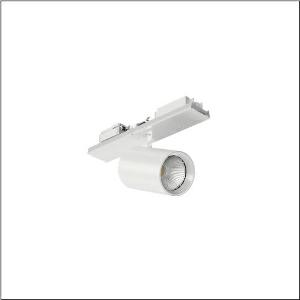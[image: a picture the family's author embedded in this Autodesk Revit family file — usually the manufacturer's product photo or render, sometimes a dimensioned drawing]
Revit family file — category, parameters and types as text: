
# Revit family: licross_spot_31_51sl127a43b
name_source: partatom
category: Lighting Fixtures
units: mm (PartAtom-declared; Revit-internal decimal feet)

## family parameters
Cut with Voids When Loaded = No
Host = Face
Light Source = No
Part Type = Normal
Room Calculation Point = No
Round Connector Dimension = Use Diameter
Shared = No

## types (1)
- --- (1 x LED, 3650 lm, 28 W, 4000K)
    Apparent Load = 28 VA
    CIE Flux Codes = 93 97 99 100 100
    Color Rendering = 90
    Color Temperature = 4000K
    Default Elevation = 1800 mm
    Description = Licross Spot 31, directional spotlight, light control with lens, of plastic, LED rated luminous flux: 3.650lm, light colour: 940, with plug, 3-pole, with phase selection, mains connection: 220..240V, AC, 50/60Hz, of aluminium, traffic white (RAL 9016), length: 300mm, diameter: 90mm, protection rating (complete): IP20, insulation class (complete): insulation class I (protective earthing), certification: CE, packaging unit: 1 piece
    Height = 175 mm
    Lamp = 1 x LED
    Lamp Light Flux = 3650 lm
    Lamp Power = 28 W
    Lamp count = 1
    Length = 90 mm
    Luminous efficacy = 130 lm/W
    Manufacturer = Siteco
    ModVariant = No
    Model = 51SL127A43B
    Mounting Place = Ceiling
    Mounting Type = Pendant
    Number of Poles = 1
    OnlyDefault = Yes
    Power Factor = 1
    Product Name = Licross Spot 31
    Product group = directional spotlight
    ProductGroupID = 905
    Protection Class = Protection class I
    Protection Degree = IP 20
    RLX_Detail_Level = 1
    RLX_Emergency_Light_Flux = 0 lm
    RLX_Emergency_Type = 0
    RLX_Emergency_Type_DB = No
    RlxData = <blob elided: 14869 chars, md5=55bfe96c>
    Socket = socket
    Standby Power = 0 W
    System Light Flux = 3650 lm
    System Power = 28 W
    Type Comments = factory setting: luminous flux: 100 % | (ON | ON | ON) | 700 mA
    Type Image = l_1245720.jpg
    URL = http://relux.com
    VarID = @adj_133901
    Voltage = 0 V
    Weight = 0.00 kg
    Width = 0 mm  [stored 0 ft]

note: [stored X ft] marks values corroborated as IEEE doubles in the binary element streams (Revit-internal decimal feet)

## geometry (parser evidence)
native form markers: Sweep x13
no freeform markers — native parametric forms only
